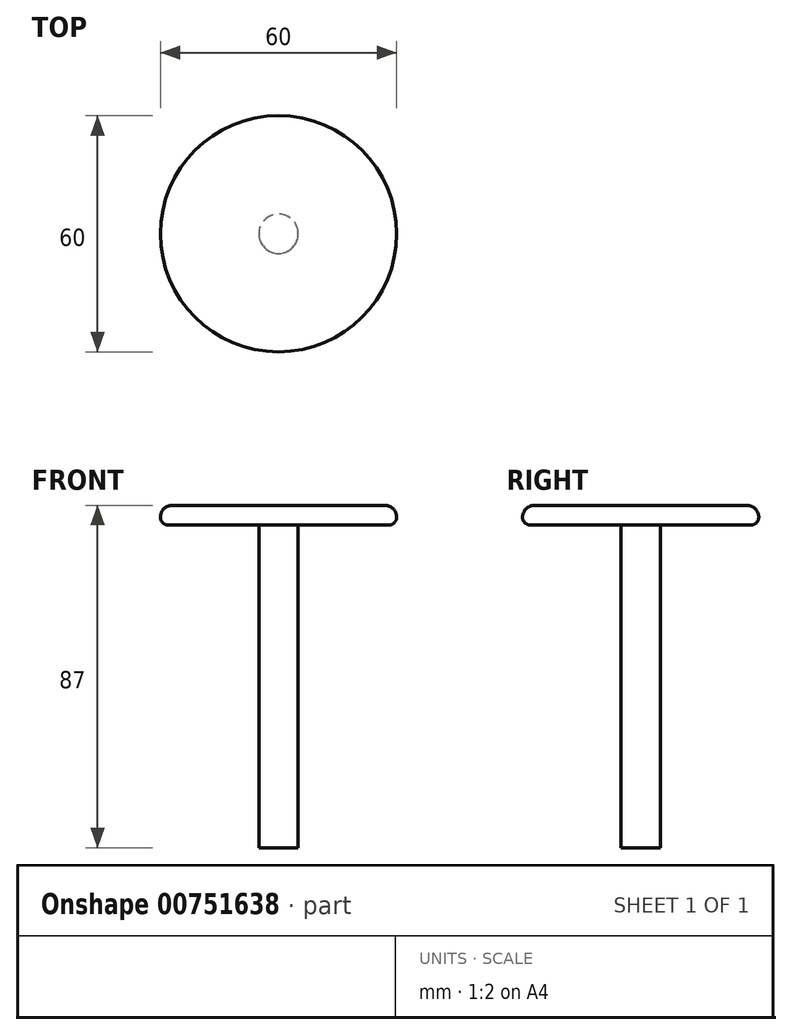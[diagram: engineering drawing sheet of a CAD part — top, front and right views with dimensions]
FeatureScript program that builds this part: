
annotation { "Feature Type Name" : "Feature", "Feature Type Description" : "" }
export const myFeature = defineFeature(function(context is Context, id is Id, definition is map)
    precondition{}
    {
        {
            var Q0;
            Q0=qCreatedBy(makeId("Top.planeOp"),FACE);
            var sketch = newSketch(context, id + "F0", { "sketchPlane" : qUnion([Q0])});
            skCircle(sketch, "E0", {"center": v(0, 0) * mm, "radius": 30 * mm});
            skSolve(sketch);
        }
        {
            var Q0;
            Q0=qSketchRegion(id+"F0",true);
            extrude(context, id + "F1", {"entities" : qUnion([Q0]), "depth" : 5 * mm});
        }
        {
            var Q0;
            Q0=makeQuery(id+"F1.opExtrude","CAP_EDGE",EDGE,{"disambiguationData":[OSD([sQuery(id+"F0.wireOp",EDGE,"E0")])],"isStart":false});
            fillet(context, id + "F2", {"entities" : qUnion([Q0]), "radius" : 3 * mm, "tangentPropagation" : true, "allowEdgeOverflow" : false});
        }
        {
            var Q0;
            Q0=makeQuery(id+"F1.opExtrude","CAP_EDGE",EDGE,{"disambiguationData":[OSD([sQuery(id+"F0.wireOp",EDGE,"E0")])],"isStart":true});
            fillet(context, id + "F3", {"entities" : qUnion([Q0]), "radius" : 2 * mm, "tangentPropagation" : true, "allowEdgeOverflow" : false});
        }
        {
            var Q0;
            Q0=makeQuery(id+"F1.opExtrude","CAP_FACE",FACE,{"disambiguationData":[OSD([sQuery(id+"F0.wireOp",EDGE,"E0")])],"isStart":true});
            var sketch = newSketch(context, id + "F4", { "sketchPlane" : qUnion([Q0])});
            skCircle(sketch, "E1", {"center": v(0, 0) * mm, "radius": 5 * mm});
            skSolve(sketch);
        }
        {
            var Q0;
            Q0=qSketchRegion(id+"F4",true);
            extrude(context, id + "F5", {"entities" : qUnion([Q0]), "operationType" : NewBodyOperationType.ADD, "depth" : 82 * mm});
        }
    });
